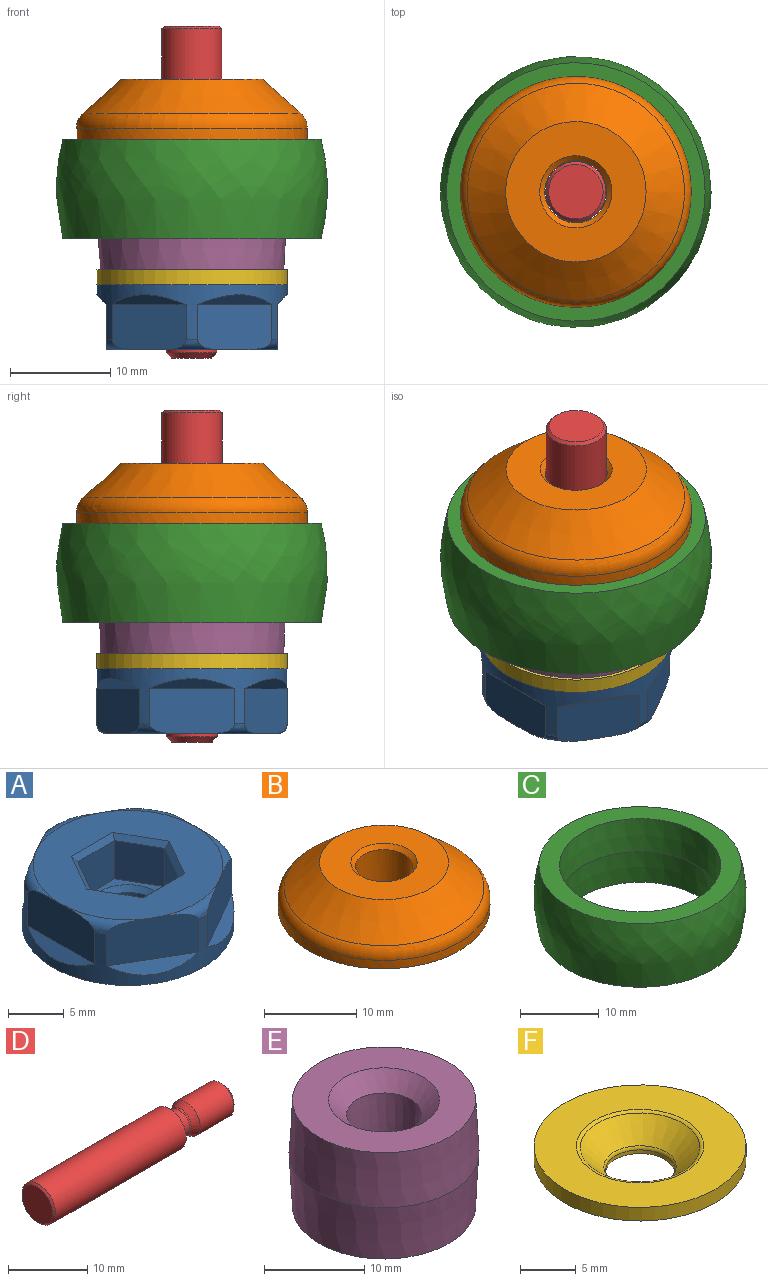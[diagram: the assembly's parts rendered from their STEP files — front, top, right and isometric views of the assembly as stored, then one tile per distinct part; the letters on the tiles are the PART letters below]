
ASSEMBLY  parts=6 mates=5
PART A: 39 faces, bbox 20.6x20.6x8 mm
  f0: torus R=8.5mm, axis (0,0,1), area 4.7mm2, adj f1,f16,f20,f30
  f1: plane 7.35x4.5mm, normal (0.5,0.87,0), area 37.1mm2, adj f0,f2,f3,f16
  f2: plane 7.35x4.24mm, normal (0.35,0.61,0.71), area 8.1mm2, adj f1,f16
  f3: torus R=8.5mm, axis (0,0,1), area 4.7mm2, adj f1,f4,f16,f20
  f4: plane 7.35x4.5mm, normal (-0.5,0.87,0), area 37.1mm2, adj f3,f5,f6,f16
  f5: plane 7.35x4.24mm, normal (-0.35,0.61,0.71), area 8.1mm2, adj f4,f16
  f6: torus R=8.5mm, axis (0,0,1), area 4.7mm2, adj f4,f7,f16,f20
  f7: plane 8.49x4.5mm, normal (-1,0,0), area 37.1mm2, adj f6,f8,f9,f16
  f8: plane 8.49x1mm, normal (-0.71,0,0.71), area 8.1mm2, adj f7,f16
  f9: torus R=8.5mm, axis (0,0,1), area 4.7mm2, adj f7,f10,f16,f20
  f10: plane 7.35x4.5mm, normal (-0.5,-0.87,0), area 37.1mm2, adj f9,f11,f12,f16
  f11: plane 7.35x4.24mm, normal (-0.35,-0.61,0.71), area 8.1mm2, adj f10,f16
  f12: torus R=8.5mm, axis (0,0,1), area 4.7mm2, adj f10,f13,f16,f20
  f13: plane 7.35x4.5mm, normal (0.5,-0.87,0), area 37.1mm2, adj f12,f14,f16,f28
  f14: plane 7.35x4.24mm, normal (0.35,-0.61,0.71), area 8.1mm2, adj f13,f16
  f15: cylinder r=3.1mm len=6.2mm, axis (0,0,1), area 44.8mm2, adj f37,f38
  f16: cylinder r=9.5mm len=19mm, axis (0,0,1), area 108.5mm2, adj f0,f1,f2,f3,f4,f5,f6,f7
  f17: plane 19x19mm, normal (0,0,-1), area 188.5mm2, adj f16,f18
  f18: cone r=5.5mm half-angle=45deg, axis (0,0,1), area 63.3mm2, adj f17,f19
  f19: plane 8x8mm, normal (0,0,-1), area 9.6mm2, adj f18,f38
  f20: plane 17x17mm, normal (0,0,1), area 155.3mm2, adj f0,f3,f6,f9,f12,f28,f31,f32
  f21: plane 4.68x4.2mm, normal (0,1,0), area 19.6mm2, adj f22,f26,f27,f35
  f22: plane 4.2x4.05mm, normal (-0.87,0.5,0), area 19.6mm2, adj f21,f23,f27,f33
  f23: plane 4.2x4.05mm, normal (-0.87,-0.5,0), area 19.6mm2, adj f22,f24,f27,f31
  f24: plane 4.68x4.2mm, normal (0,-1,0), area 19.6mm2, adj f23,f25,f27,f32
  f25: plane 4.2x4.05mm, normal (0.87,-0.5,0), area 19.6mm2, adj f24,f26,f27,f34
  f26: plane 4.2x4.05mm, normal (0.87,0.5,0), area 19.6mm2, adj f21,f25,f27,f36
  f27: plane 9.35x8.1mm, normal (0,0,1), area 16.1mm2, adj f21,f22,f23,f24,f25,f26,f37
  f28: torus R=8.5mm, axis (0,0,1), area 4.7mm2, adj f13,f16,f20,f30
  f29: plane 8.49x1mm, normal (0.71,0,0.71), area 8.1mm2, adj f16,f30
  f30: plane 8.49x4.5mm, normal (1,0,0), area 37.1mm2, adj f0,f16,f28,f29
  f31: plane 4.55x2.92mm, normal (-0.61,-0.35,0.71), area 3.5mm2, adj f20,f23,f32,f33
  f32: plane 5.25x0.5mm, normal (0,-0.71,0.71), area 3.5mm2, adj f20,f24,f31,f34
  f33: plane 4.55x2.92mm, normal (-0.61,0.35,0.71), area 3.5mm2, adj f20,f22,f31,f35
  f34: plane 4.55x2.92mm, normal (0.61,-0.35,0.71), area 3.5mm2, adj f20,f25,f32,f36
  f35: plane 5.25x0.5mm, normal (0,0.71,0.71), area 3.5mm2, adj f20,f21,f33,f36
  f36: plane 4.55x2.92mm, normal (0.61,0.35,0.71), area 3.5mm2, adj f20,f26,f34,f35
  f37: cone r=3.1mm half-angle=45deg, axis (0,0,1), area 14.9mm2, adj f15,f27
  f38: cone r=3.6mm half-angle=45deg, axis (0,0,-1), area 14.9mm2, adj f15,f19
PART B: 10 faces, bbox 24.9x24.9x7.5 mm
  f0: cylinder r=11.5mm len=23mm, axis (0,0,1), area 79.6mm2, adj f1,f9
  f1: plane 23x23mm, normal (0,0,-1), area 320.4mm2, adj f0,f2
  f2: cone r=5.5mm half-angle=45deg, axis (0,0,1), area 63.3mm2, adj f1,f3
  f3: plane 8x8mm, normal (0,0,-1), area 9.6mm2, adj f2,f7
  f4: cylinder r=3.1mm len=6.5mm, axis (0,0,1), area 126.6mm2, adj f7,f8
  f5: plane 14x14mm, normal (0,0,1), area 113.2mm2, adj f6,f8
  f6: cone r=11.5mm half-angle=48.4deg, axis (0,0,-1), area 286.9mm2, adj f5,f9
  f7: cone r=3.6mm half-angle=45deg, axis (0,0,-1), area 14.9mm2, adj f3,f4
  f8: cone r=3.1mm half-angle=45deg, axis (0,0,1), area 14.9mm2, adj f4,f5
  f9: torus R=9.5mm, axis (0,0,-1), area 119.6mm2, adj f0,f6
PART C: 5 faces, bbox 27x27x9.9 mm
  f0: plane 25.76x25.76mm, normal (0,0,1), area 190.3mm2, adj f1,f4
  f1: revolved ~27x27mm, area 835.5mm2, adj f0,f2
  f2: plane 25.76x25.76mm, normal (0,0,-1), area 190.3mm2, adj f1,f3
  f3: cone r=10mm half-angle=3deg, axis (0,0,-1), area 315.5mm2, adj f2,f4
  f4: cone r=10.26mm half-angle=3deg, axis (0,0,1), area 315.5mm2, adj f0,f3
PART D: 11 faces, bbox 33.1x6x6 mm
  f0: cone r=3mm half-angle=45deg, axis (1,0,0), area 7.4mm2, adj f1,f10
  f1: cylinder r=3mm len=23.3mm, axis (1,0,0), area 439.2mm2, adj f0,f9
  f2: torus R=2.38mm, axis (-1,0,0), area 10.1mm2, adj f3,f9
  f3: cylinder r=1.88mm len=3.75mm, axis (1,0,0), area 14.7mm2, adj f2,f4
  f4: torus R=2.38mm, axis (-1,0,0), area 3.1mm2, adj f3,f5
  f5: cone r=2.5mm half-angle=30deg, axis (1,0,0), area 15.6mm2, adj f4,f6
  f6: cylinder r=2.5mm len=6.03mm, axis (1,0,0), area 94.8mm2, adj f5,f7
  f7: cone r=2mm half-angle=45deg, axis (-1,0,0), area 10mm2, adj f6,f8
  f8: plane 4x4mm, normal (1,0,0), area 12.6mm2, adj f7
  f9: plane 6x6mm, normal (1,0,0), area 10.6mm2, adj f1,f2
  f10: plane 5.42x5.42mm, normal (-1,0,0), area 23.1mm2, adj f0
PART E: 8 faces, bbox 19x19x13 mm
  f0: plane 18.32x18.32mm, normal (0,0,1), area 166.8mm2, adj f1,f7
  f1: cone r=9.5mm half-angle=3deg, axis (0,0,-1), area 381.6mm2, adj f0,f2
  f2: cone r=9.5mm half-angle=3deg, axis (0,0,1), area 381.6mm2, adj f1,f3
  f3: plane 18.32x18.32mm, normal (0,0,-1), area 166.8mm2, adj f2,f4
  f4: cone r=5.55mm half-angle=45deg, axis (0,0,-1), area 74.5mm2, adj f3,f5
  f5: cone r=3.5mm half-angle=3deg, axis (0,0,-1), area 107.1mm2, adj f4,f6
  f6: cone r=3.5mm half-angle=3deg, axis (0,0,1), area 107.1mm2, adj f5,f7
  f7: cone r=5.55mm half-angle=45deg, axis (0,0,1), area 74.5mm2, adj f0,f6
PART F: 9 faces, bbox 19x19x3 mm
  f0: cylinder r=9.5mm len=19mm, axis (0,0,1), area 89.5mm2, adj f1,f6
  f1: plane 19x19mm, normal (0,0,-1), area 188.5mm2, adj f0,f2
  f2: cone r=5.5mm half-angle=45deg, axis (0,0,1), area 63.3mm2, adj f1,f3
  f3: plane 8x8mm, normal (0,0,-1), area 20.1mm2, adj f2,f4
  f4: cylinder r=3.1mm len=6.2mm, axis (0,0,1), area 7.7mm2, adj f3,f7
  f5: cone r=5.5mm half-angle=45deg, axis (0,0,1), area 80.5mm2, adj f7,f8
  f6: plane 19x19mm, normal (0,0,1), area 181.2mm2, adj f0,f8
  f7: torus R=3.6mm, axis (0,0,-1), area 7.8mm2, adj f4,f5
  f8: torus R=5.71mm, axis (0,0,1), area 13.6mm2, adj f5,f6
PLACE A rot(axis=(1,0,0),180deg) t=(0,0,-23)mm
PLACE B t=(0,0,-3.75)mm
PLACE C t=(0,0,-10.95)mm
PLACE D rot(axis=(0.71,0,-0.71),180deg) t=(0,0,6.7)mm
PLACE E t=(0,0,-12.5)mm
PLACE F rot(axis=(1,0,0),180deg) t=(0,0,-19)mm
MATE fastened F.f0 <-> E.f1  axis (0,0,1) through (0,0,-19)mm
MATE fastened F.f0 <-> A.f0  axis (0,0,-1) through (0,0,-20.5)mm
MATE slider D.f0 <-> B.f0  axis (0,0,-1) through (0,0,-6.65)mm
MATE fastened E.f1 <-> B.f0  axis (0,0,1) through (0,0,-6)mm
MATE fastened C.f3 <-> B.f0  axis (0,0,1) through (0,0,-6)mm
